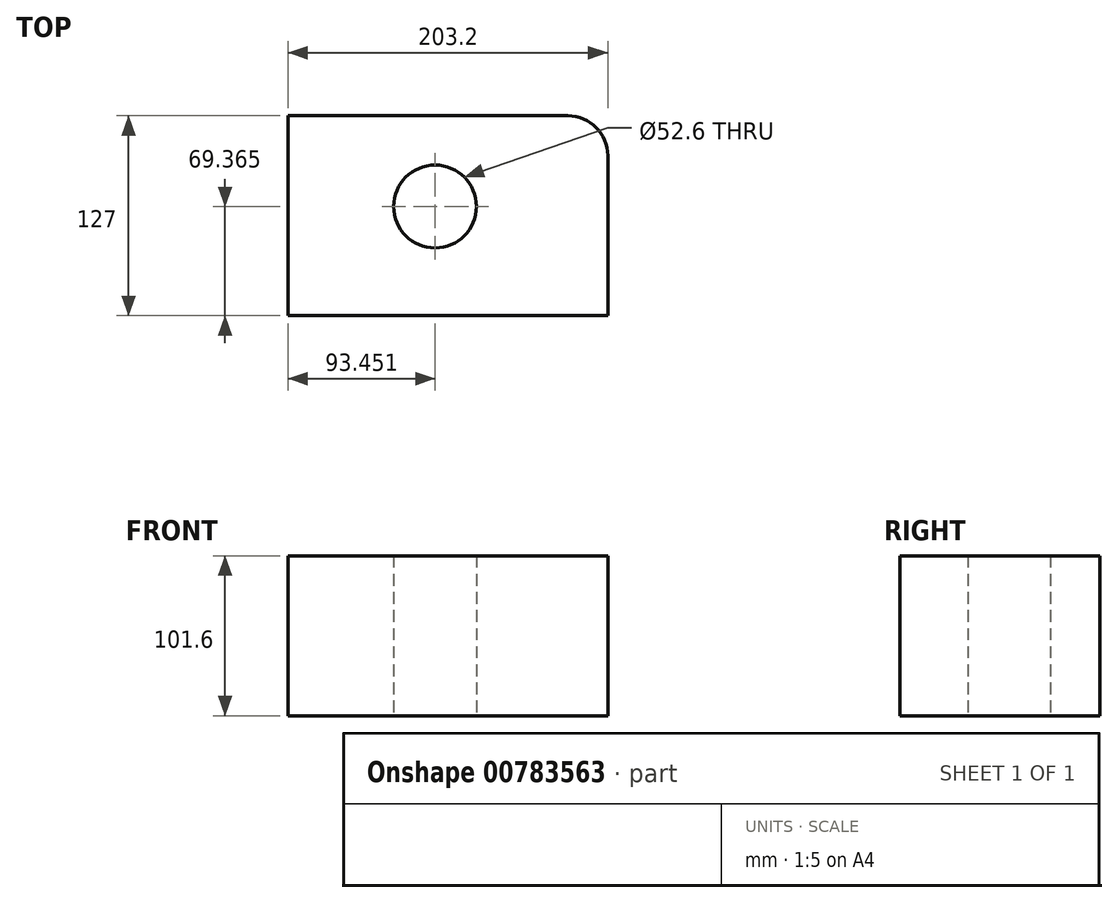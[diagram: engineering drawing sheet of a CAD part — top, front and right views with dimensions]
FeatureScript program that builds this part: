
annotation { "Feature Type Name" : "Feature", "Feature Type Description" : "" }
export const myFeature = defineFeature(function(context is Context, id is Id, definition is map)
    precondition{}
    {
        {
            var Q0;
            Q0=qCreatedBy(makeId("Top.planeOp"),FACE);
            var sketch = newSketch(context, id + "F0", { "sketchPlane" : qUnion([Q0])});
            skLineSegment(sketch, "E0.bottom", {"start": v(0, 0) * mm, "end": v(203.2, 0) * mm});
            skLineSegment(sketch, "E0.top", {"start": v(0, 127) * mm, "end": v(177.8, 127) * mm});
            skLineSegment(sketch, "E0.left", {"start": v(0, 0) * mm, "end": v(0, 127) * mm});
            skLineSegment(sketch, "E0.right", {"start": v(203.2, 0) * mm, "end": v(203.2, 101.6) * mm});
            skPoint(sketch, "E1.visualSharp", {"position": v(203.2, 127) * mm});
            skArc(sketch, "E1.filletArc", {"start": v(203.2, 101.6) * mm, "mid": v(195.76, 119.56) * mm, "end": v(177.8, 127) * mm});
            skCircle(sketch, "E2", {"center": v(93.45, 69.37) * mm, "radius": 26.3 * mm});
            skSolve(sketch);
        }
        {
            var Q0;
            Q0=makeQuery(id+"F0.imprint","IMPRINT",FACE,{"disambiguationData":[TD([[makeQuery(id+"F0.imprint","IMPRINT",EDGE,{"derivedFrom":sQuery(id+"F0.wireOp",EDGE,"E0.bottom")}),1.0]])]});
            extrude(context, id + "F1", {"entities" : qUnion([Q0]), "depth" : 101.6 * mm, "offsetDistance" : 25.4 * mm});
        }
    });
